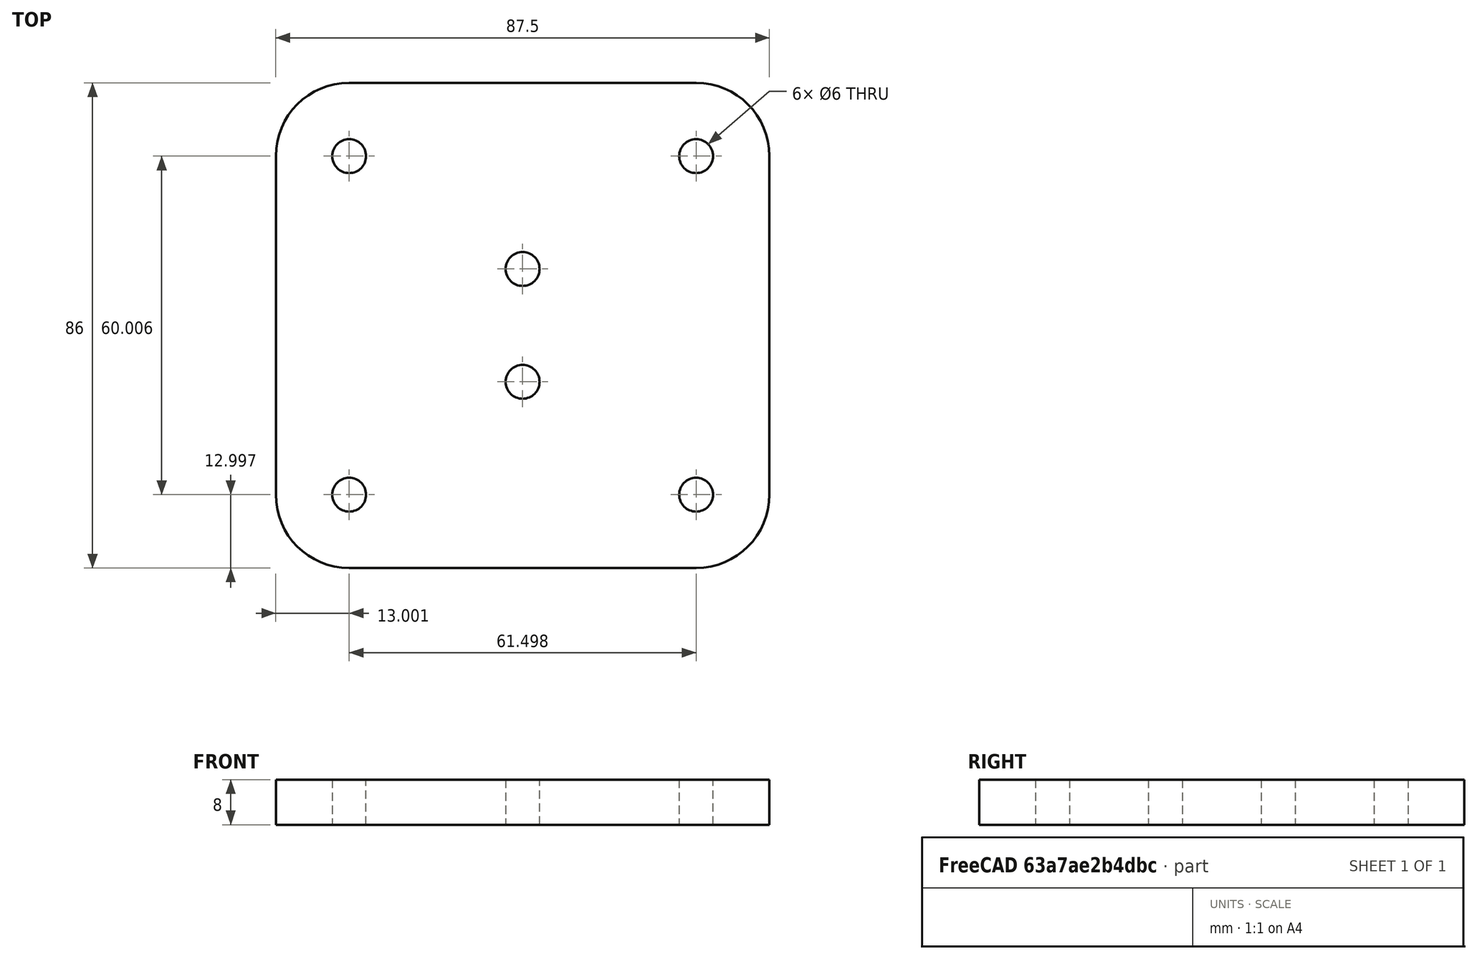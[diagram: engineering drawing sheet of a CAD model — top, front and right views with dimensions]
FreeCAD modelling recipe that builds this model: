
FCSTD DOCUMENT  (FreeCAD 0.14R3703 (Git))
Label: pletina_brazo
License: CC-BY 3.0
LicenseURL: http://creativecommons.org/licenses/by/3.0/
objects: Sketcher::SketchObject×1, PartDesign::Pad×1, Part::Feature×1
note: 4 computed .brp shape members not serialized (recipe doc carries the construction recipe); baked Part::Feature solids carry a one-line shape summary decoded from their .brp

FEATURE [Sketcher::SketchObject] Sketch
  sketch-geometry (14):
    g0: LineSegment StartX=-30.7492 StartY=43.0028 StartZ=0 EndX=30.7492 EndY=43.0028 EndZ=0
    g1: LineSegment StartX=43.7493 StartY=30.0028 StartZ=0 EndX=43.7493 EndY=-30.0028 EndZ=0
    g2: LineSegment StartX=30.7492 StartY=-43.0028 StartZ=0 EndX=-30.7492 EndY=-43.0028 EndZ=0
    g3: LineSegment StartX=-43.7493 StartY=-30.0028 StartZ=0 EndX=-43.7493 EndY=30.0028 EndZ=0
    g4: ArcOfCircle CenterX=-30.7492 CenterY=30.0028 CenterZ=0 NormalX=0 NormalY=0 NormalZ=1 Radius=13 StartAngle=1.5708 EndAngle=3.14159
    g5: ArcOfCircle CenterX=30.7492 CenterY=30.0028 CenterZ=0 NormalX=0 NormalY=0 NormalZ=1 Radius=13 StartAngle=0 EndAngle=1.5708
    g6: ArcOfCircle CenterX=30.7492 CenterY=-30.0028 CenterZ=0 NormalX=0 NormalY=0 NormalZ=1 Radius=13 StartAngle=4.71239 EndAngle=6.28319
    g7: ArcOfCircle CenterX=-30.7492 CenterY=-30.0028 CenterZ=0 NormalX=0 NormalY=0 NormalZ=1 Radius=13 StartAngle=3.14159 EndAngle=4.71239
    g8: Circle CenterX=-30.7492 CenterY=30.0028 CenterZ=0 NormalX=0 NormalY=0 NormalZ=1 Radius=3
    g9: Circle CenterX=30.7492 CenterY=30.0028 CenterZ=0 NormalX=0 NormalY=0 NormalZ=1 Radius=3
    g10: Circle CenterX=-30.7492 CenterY=-30.0028 CenterZ=0 NormalX=0 NormalY=0 NormalZ=1 Radius=3
    g11: Circle CenterX=30.7492 CenterY=-30.0028 CenterZ=0 NormalX=0 NormalY=0 NormalZ=1 Radius=3
    g12: Circle CenterX=0 CenterY=10 CenterZ=0 NormalX=0 NormalY=0 NormalZ=1 Radius=3
    g13: Circle CenterX=0 CenterY=-10 CenterZ=0 NormalX=0 NormalY=0 NormalZ=1 Radius=3
  constraints (33):
    c: Horizontal(g0)
    c: Horizontal(g2)
    c: Vertical(g1)
    c: Vertical(g3)
    c: Tangent(g0,g4)
    c: Tangent(g3,g4)
    c: Tangent(g0,g5)
    c: Tangent(g1,g5)
    c: Tangent(g1,g6)
    c: Tangent(g2,g6)
    c: Tangent(g2,g7)
    c: Tangent(g3,g7)
    c: Radius(g5) = 13
    c: DistanceX(g3,g1) = 87.4985
    c: DistanceY(g0,g2) = -86.0056
    c: Symmetric(g0,g0,g-2)
    c: Symmetric(g3,g3,g-1)
    c: Radius(g6) = 13
    c: Radius(g7) = 13
    c: Radius(g4) = 13
    c: Radius(g8) = 3
    c: Equal(g8,g9)
    c: Equal(g9,g11)
    c: Equal(g11,g10)
    c: Equal(g12,g13)
    c: Equal(g13,g9)
    c: Coincident(g11,g6)
    c: Coincident(g9,g5)
    c: Coincident(g8,g4)
    c: Coincident(g10,g7)
    c: DistanceY(g12,g13) = -20
    c: Symmetric(g12,g13,g-1)
    c: PointOnObject(g12,g-2)
FEATURE [PartDesign::Pad] Pad
  Length = 8
  Length2 = 100
  Sketch = -> Sketch
  Type = 0
FEATURE [Part::Feature] Pad001  label="pletina_brazo"
  shape: bbox 87.5 x 86.01 x 8 mm, 16 faces (baked)
